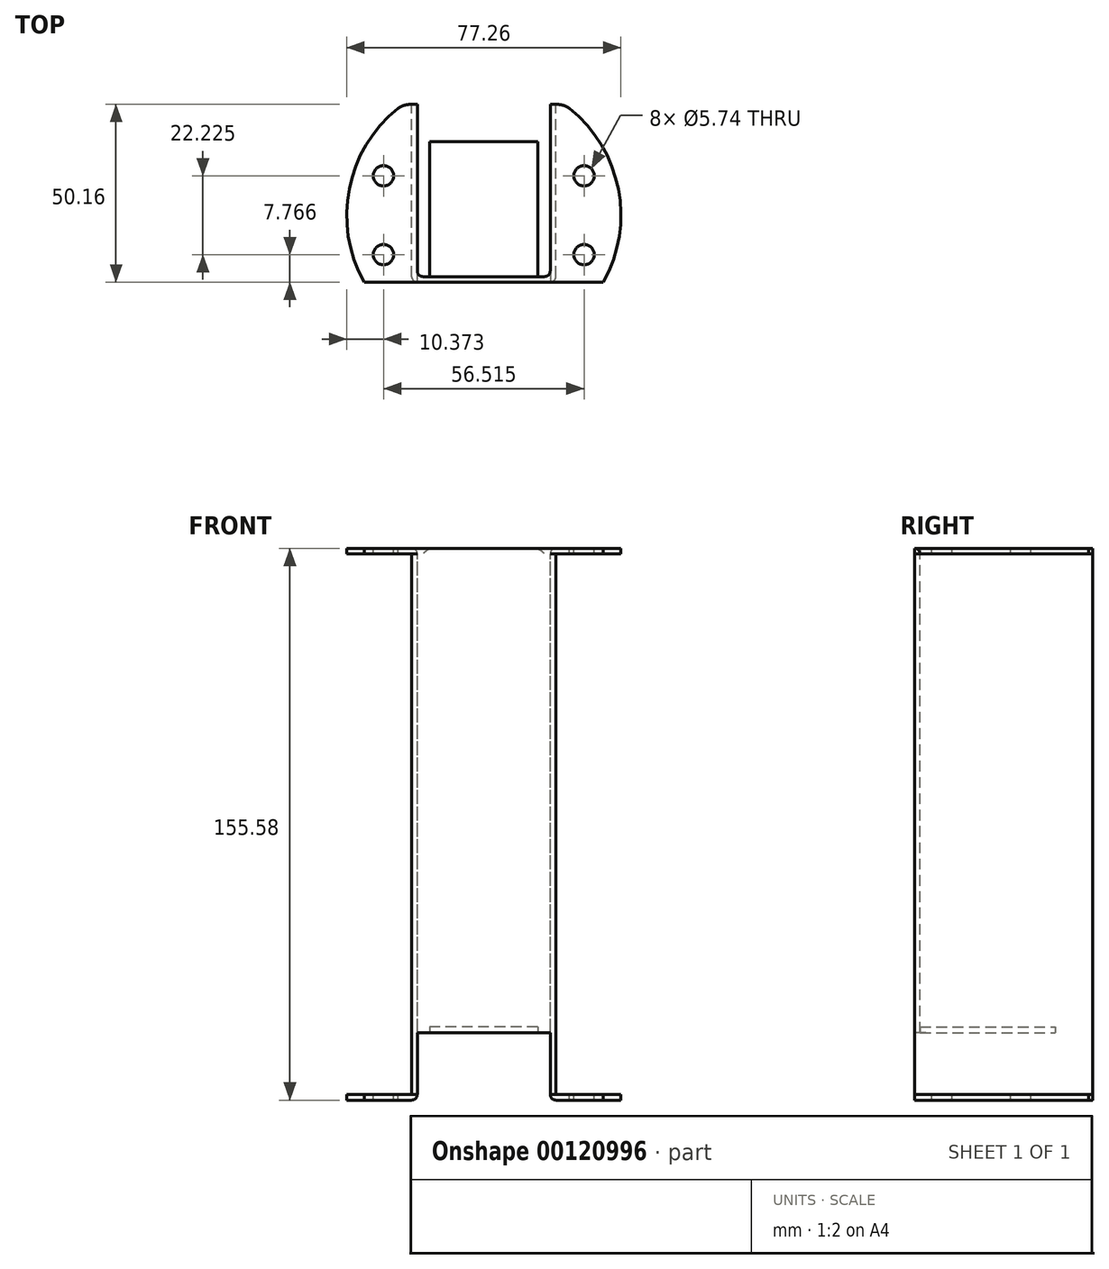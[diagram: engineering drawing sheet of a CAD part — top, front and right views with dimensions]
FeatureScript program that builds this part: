
annotation { "Feature Type Name" : "Feature", "Feature Type Description" : "" }
export const myFeature = defineFeature(function(context is Context, id is Id, definition is map)
    precondition{}
    {
        {
            var Q0;
            Q0=qCreatedBy(makeId("Top.planeOp"),FACE);
            var sketch = newSketch(context, id + "F0", { "sketchPlane" : qUnion([Q0])});
            skLineSegment(sketch, "E0", {"start": v(0, 0) * mm, "end": v(20.32, 0) * mm});
            skLineSegment(sketch, "E1", {"start": v(20.32, 0) * mm, "end": v(20.32, 50.17) * mm});
            skLineSegment(sketch, "E2", {"start": v(20.32, 50.17) * mm, "end": v(18.73, 50.17) * mm});
            skLineSegment(sketch, "E3", {"start": v(18.73, 50.17) * mm, "end": v(18.73, 1.59) * mm});
            skLineSegment(sketch, "E4", {"start": v(18.73, 1.59) * mm, "end": v(-18.73, 1.59) * mm});
            skLineSegment(sketch, "E5", {"start": v(-18.73, 1.59) * mm, "end": v(-18.73, 50.16) * mm});
            skLineSegment(sketch, "E6", {"start": v(-18.73, 50.16) * mm, "end": v(-20.32, 50.16) * mm});
            skLineSegment(sketch, "E7", {"start": v(-20.32, 50.17) * mm, "end": v(-20.32, 0) * mm});
            skLineSegment(sketch, "E8", {"start": v(-20.32, 0) * mm, "end": v(0, 0) * mm});
            skLineSegment(sketch, "E9", {"start": v(18.73, 1.59) * mm, "end": v(18.73, 0) * mm, "construction": true});
            skLineSegment(sketch, "E10", {"start": v(20.32, 0) * mm, "end": v(33.7, 0) * mm});
            skLineSegment(sketch, "E11", {"start": v(20.32, 49.04) * mm, "end": v(24.14, 49.04) * mm});
            skArc(sketch, "E12", {"start": v(33.7, 0) * mm, "mid": v(37.92, 26.27) * mm, "end": v(24.14, 49.04) * mm});
            skCircle(sketch, "E13", {"center": v(28.26, 30) * mm, "radius": 2.87 * mm});
            skCircle(sketch, "E14", {"center": v(28.26, 7.77) * mm, "radius": 2.87 * mm});
            skLineSegment(sketch, "E15", {"start": v(28.26, 30) * mm, "end": v(28.26, 7.77) * mm, "construction": true});
            skLineSegment(sketch, "E16", {"start": v(38.63, 18.88) * mm, "end": v(20.32, 18.88) * mm, "construction": true});
            skLineSegment(sketch, "E17", {"start": v(38.63, 18.88) * mm, "end": v(38.63, 5.02) * mm, "construction": true});
            skPoint(sketch, "E18", {"position": v(28.26, 18.88) * mm});
            skArc(sketch, "E19", {"start": v(24.14, 49.04) * mm, "mid": v(22.31, 49.88) * mm, "end": v(20.32, 50.17) * mm});
            skSolve(sketch);
        }
        {
            var Q0;
            {var subQ3=sQuery(id+"F0.wireOp",EDGE,"E0");Q0=makeQuery(id+"F0.imprint","IMPRINT",FACE,{"disambiguationData":[TD([[makeQuery(id+"F0.imprint","IMPRINT",EDGE,{"derivedFrom":subQ3}),1.0]])]});}
            extrude(context, id + "F1", {"entities" : qUnion([Q0]), "oppositeDirection" : true, "depth" : 136.53 * mm});
        }
        {
            var Q0;
            Q0=makeQuery(id+"F1.opExtrude","CAP_FACE",FACE,{"disambiguationData":[OSD([sQuery(id+"F0.wireOp",EDGE,"E0"),sQuery(id+"F0.wireOp",EDGE,"E1"),sQuery(id+"F0.wireOp",EDGE,"E2"),sQuery(id+"F0.wireOp",EDGE,"E3"),sQuery(id+"F0.wireOp",EDGE,"E4"),sQuery(id+"F0.wireOp",EDGE,"E5"),sQuery(id+"F0.wireOp",EDGE,"E6"),sQuery(id+"F0.wireOp",EDGE,"E7"),sQuery(id+"F0.wireOp",EDGE,"E8")])],"isStart":false});
            var sketch = newSketch(context, id + "F2", { "sketchPlane" : qUnion([Q0])});
            skLineSegment(sketch, "E20.0.0", {"start": v(20.32, 0) * mm, "end": v(-20.32, 0) * mm});
            skLineSegment(sketch, "E20.0.1", {"start": v(-20.32, 0) * mm, "end": v(-20.32, -50.17) * mm});
            skLineSegment(sketch, "E20.0.2", {"start": v(-20.32, -50.16) * mm, "end": v(-18.73, -50.16) * mm});
            skLineSegment(sketch, "E20.0.3", {"start": v(-18.73, -50.17) * mm, "end": v(-18.73, -1.59) * mm});
            skLineSegment(sketch, "E20.0.4", {"start": v(-18.73, -1.59) * mm, "end": v(18.73, -1.59) * mm});
            skLineSegment(sketch, "E20.0.5", {"start": v(18.73, -1.59) * mm, "end": v(18.73, -50.17) * mm});
            skLineSegment(sketch, "E20.0.6", {"start": v(18.73, -50.17) * mm, "end": v(20.32, -50.17) * mm});
            skLineSegment(sketch, "E20.0.7", {"start": v(20.32, -50.17) * mm, "end": v(20.32, 0) * mm});
            skLineSegment(sketch, "E21", {"start": v(-18.73, -1.59) * mm, "end": v(-18.73, 0) * mm});
            skLineSegment(sketch, "E22", {"start": v(18.73, -1.59) * mm, "end": v(18.73, 0) * mm});
            skSolve(sketch);
        }
        {
            var Q0;
            {var subQ1=sQuery(id+"F2.wireOp",EDGE,"E20.0.1");Q0=makeQuery(id+"F2.imprint","IMPRINT",FACE,{"disambiguationData":[TD([[makeQuery(id+"F2.imprint","IMPRINT",EDGE,{"derivedFrom":subQ1}),-1.0]])]});}
            var Q1;
            Q1=makeQuery(id+"F2.imprint","IMPRINT",FACE,{"disambiguationData":[TD([[makeQuery(id+"F2.imprint","IMPRINT",EDGE,{"derivedFrom":sQuery(id+"F2.wireOp",EDGE,"E20.0.5")}),-1.0]])]});
            extrude(context, id + "F3", {"entities" : qUnion([Q0, Q1]), "operationType" : NewBodyOperationType.ADD, "depth" : 19.05 * mm});
        }
        {
            var Q0;
            {var subQ0=sQuery(id+"F0.wireOp",EDGE,"E10");Q0=makeQuery(id+"F0.imprint","IMPRINT",FACE,{"disambiguationData":[TD([[makeQuery(id+"F0.imprint","IMPRINT",EDGE,{"derivedFrom":subQ0}),1.0]])]});}
            var Q1;
            {var subQ2=sQuery(id+"F0.wireOp",EDGE,"E11");Q1=makeQuery(id+"F0.imprint","IMPRINT",FACE,{"disambiguationData":[TD([[makeQuery(id+"F0.imprint","IMPRINT",EDGE,{"derivedFrom":subQ2}),1.0]])]});}
            extrude(context, id + "F4", {"entities" : qUnion([Q0, Q1]), "oppositeDirection" : true, "depth" : 1.59 * mm});
        }
        {
            var Q0;
            Q0=makeQuery(id+"F4.opExtrude","SWEPT_BODY",BODY,{"disambiguationData":[OSD([sQuery(id+"F0.wireOp",EDGE,"E1"),sQuery(id+"F0.wireOp",EDGE,"E10"),sQuery(id+"F0.wireOp",EDGE,"E12"),sQuery(id+"F0.wireOp",EDGE,"E13"),sQuery(id+"F0.wireOp",EDGE,"E14"),sQuery(id+"F0.wireOp",EDGE,"E19")])]});
            var Q1;
            Q1=qCreatedBy(makeId("Right.planeOp"),FACE);
            mirror(context, id + "F5", {"entities" : qUnion([Q0]), "mirrorPlane" : qUnion([Q1])});
        }
        {
            var Q0;
            Q0=makeQuery(id+"F5.opPattern","COPY",BODY,{"derivedFrom":makeQuery(id+"F4.opExtrude","SWEPT_BODY",BODY,{"disambiguationData":[OSD([sQuery(id+"F0.wireOp",EDGE,"E1"),sQuery(id+"F0.wireOp",EDGE,"E10"),sQuery(id+"F0.wireOp",EDGE,"E12"),sQuery(id+"F0.wireOp",EDGE,"E13"),sQuery(id+"F0.wireOp",EDGE,"E14"),sQuery(id+"F0.wireOp",EDGE,"E19")])]}),"instanceName":"1"});
            var Q1;
            Q1=makeQuery(id+"F4.opExtrude","SWEPT_BODY",BODY,{"disambiguationData":[OSD([sQuery(id+"F0.wireOp",EDGE,"E1"),sQuery(id+"F0.wireOp",EDGE,"E10"),sQuery(id+"F0.wireOp",EDGE,"E12"),sQuery(id+"F0.wireOp",EDGE,"E13"),sQuery(id+"F0.wireOp",EDGE,"E14"),sQuery(id+"F0.wireOp",EDGE,"E19")])]});
            var Q2;
            Q2=makeQuery(id+"F5.opPattern","COPY",VERTEX,{"derivedFrom":makeQuery(id+"F4.opExtrude","CAP_VERTEX",VERTEX,{"disambiguationData":[OSD([sQuery(id+"F0.wireOp",EDGE,"E0"),sQuery(id+"F0.wireOp",EDGE,"E1"),sQuery(id+"F0.wireOp",EDGE,"E10")])],"isStart":false}),"instanceName":"1"});
            var Q3;
            Q3=makeQuery(id+"F3.opExtrude","CAP_VERTEX",VERTEX,{"disambiguationData":[OSD([sQuery(id+"F2.wireOp",EDGE,"E20.0.0"),sQuery(id+"F2.wireOp",EDGE,"E20.0.1")])],"isStart":false});
            var Q4;
            Q4=makeQuery(id+"F5.opPattern","COPY",VERTEX,{"derivedFrom":makeQuery(id+"F4.opExtrude","CAP_VERTEX",VERTEX,{"disambiguationData":[OSD([sQuery(id+"F0.wireOp",EDGE,"E0"),sQuery(id+"F0.wireOp",EDGE,"E1"),sQuery(id+"F0.wireOp",EDGE,"E10")])],"isStart":false}),"instanceName":"1"});
            var Q5;
            Q5=makeQuery(id+"F3.opExtrude","CAP_VERTEX",VERTEX,{"disambiguationData":[OSD([sQuery(id+"F2.wireOp",EDGE,"E20.0.0"),sQuery(id+"F2.wireOp",EDGE,"E20.0.1")])],"isStart":false});
            transform(context, id + "F6", {"entities" : qUnion([Q0, Q1]), "transformType" : TransformType.TRANSLATION_ENTITY, "oppositeDirectionEntity" : false, "transformLine" : qUnion([Q2, Q3]), "makeCopy" : true});
        }
        {
            var Q0;
            Q0=makeQuery(id+"F1.opExtrude","SWEPT_BODY",BODY,{"disambiguationData":[OSD([sQuery(id+"F0.wireOp",EDGE,"E0"),sQuery(id+"F0.wireOp",EDGE,"E1"),sQuery(id+"F0.wireOp",EDGE,"E2"),sQuery(id+"F0.wireOp",EDGE,"E3"),sQuery(id+"F0.wireOp",EDGE,"E4"),sQuery(id+"F0.wireOp",EDGE,"E5"),sQuery(id+"F0.wireOp",EDGE,"E6"),sQuery(id+"F0.wireOp",EDGE,"E7"),sQuery(id+"F0.wireOp",EDGE,"E8")])]});
            var Q1;
            Q1=makeQuery(id+"F4.opExtrude","SWEPT_BODY",BODY,{"disambiguationData":[OSD([sQuery(id+"F0.wireOp",EDGE,"E1"),sQuery(id+"F0.wireOp",EDGE,"E10"),sQuery(id+"F0.wireOp",EDGE,"E12"),sQuery(id+"F0.wireOp",EDGE,"E13"),sQuery(id+"F0.wireOp",EDGE,"E14"),sQuery(id+"F0.wireOp",EDGE,"E19")])]});
            var Q2;
            Q2=makeQuery(id+"F5.opPattern","COPY",BODY,{"derivedFrom":makeQuery(id+"F4.opExtrude","SWEPT_BODY",BODY,{"disambiguationData":[OSD([sQuery(id+"F0.wireOp",EDGE,"E1"),sQuery(id+"F0.wireOp",EDGE,"E10"),sQuery(id+"F0.wireOp",EDGE,"E12"),sQuery(id+"F0.wireOp",EDGE,"E13"),sQuery(id+"F0.wireOp",EDGE,"E14"),sQuery(id+"F0.wireOp",EDGE,"E19")])]}),"instanceName":"1"});
            var Q3;
            Q3=makeQuery(id+"F6.opPattern","COPY",BODY,{"derivedFrom":makeQuery(id+"F4.opExtrude","SWEPT_BODY",BODY,{"disambiguationData":[OSD([sQuery(id+"F0.wireOp",EDGE,"E1"),sQuery(id+"F0.wireOp",EDGE,"E10"),sQuery(id+"F0.wireOp",EDGE,"E12"),sQuery(id+"F0.wireOp",EDGE,"E13"),sQuery(id+"F0.wireOp",EDGE,"E14"),sQuery(id+"F0.wireOp",EDGE,"E19")])]}),"instanceName":"1"});
            var Q4;
            Q4=makeQuery(id+"F6.opPattern","COPY",BODY,{"derivedFrom":makeQuery(id+"F5.opPattern","COPY",BODY,{"derivedFrom":makeQuery(id+"F4.opExtrude","SWEPT_BODY",BODY,{"disambiguationData":[OSD([sQuery(id+"F0.wireOp",EDGE,"E1"),sQuery(id+"F0.wireOp",EDGE,"E10"),sQuery(id+"F0.wireOp",EDGE,"E12"),sQuery(id+"F0.wireOp",EDGE,"E13"),sQuery(id+"F0.wireOp",EDGE,"E14"),sQuery(id+"F0.wireOp",EDGE,"E19")])]}),"instanceName":"1"}),"instanceName":"1"});
            booleanBodies(context, id + "F7", {"operationType" : BooleanOperationType.UNION, "tools" : qUnion([Q0, Q1, Q2, Q3, Q4])});
        }
        {
            var Q0;
            Q0=makeQuery(id+"F1.opExtrude","CAP_FACE",FACE,{"disambiguationData":[OSD([sQuery(id+"F0.wireOp",EDGE,"E0"),sQuery(id+"F0.wireOp",EDGE,"E1"),sQuery(id+"F0.wireOp",EDGE,"E2"),sQuery(id+"F0.wireOp",EDGE,"E3"),sQuery(id+"F0.wireOp",EDGE,"E4"),sQuery(id+"F0.wireOp",EDGE,"E5"),sQuery(id+"F0.wireOp",EDGE,"E6"),sQuery(id+"F0.wireOp",EDGE,"E7"),sQuery(id+"F0.wireOp",EDGE,"E8")])],"isStart":false});
            var sketch = newSketch(context, id + "F8", { "sketchPlane" : qUnion([Q0])});
            skLineSegment(sketch, "E23.bottom", {"start": v(-15.24, -1.59) * mm, "end": v(15.24, -1.59) * mm});
            skLineSegment(sketch, "E23.top", {"start": v(-15.24, -39.69) * mm, "end": v(15.24, -39.69) * mm});
            skLineSegment(sketch, "E23.left", {"start": v(-15.24, -1.59) * mm, "end": v(-15.24, -39.69) * mm});
            skLineSegment(sketch, "E23.right", {"start": v(15.24, -1.59) * mm, "end": v(15.24, -39.69) * mm});
            skPoint(sketch, "E24", {"position": v(0, -1.59) * mm});
            skSolve(sketch);
        }
        {
            var Q0;
            Q0=makeQuery(id+"F8.imprint","IMPRINT",FACE,{"disambiguationData":[TD([[makeQuery(id+"F8.imprint","IMPRINT",EDGE,{"derivedFrom":sQuery(id+"F8.wireOp",EDGE,"E23.bottom")}),1.0]])]});
            extrude(context, id + "F9", {"entities" : qUnion([Q0]), "operationType" : NewBodyOperationType.ADD, "oppositeDirection" : true, "depth" : 1.59 * mm});
        }
        {
            var Q0;
            Q0=makeQuery(id+"F5.opPattern","COPY",EDGE,{"derivedFrom":makeQuery(id+"F4.opExtrude","CAP_EDGE",EDGE,{"disambiguationData":[OSD([sQuery(id+"F0.wireOp",EDGE,"E1")])],"isStart":false}),"instanceName":"1"});
            var Q1;
            Q1=makeQuery(id+"F1.opExtrude","CAP_EDGE",EDGE,{"disambiguationData":[OSD([sQuery(id+"F0.wireOp",EDGE,"E5")])],"isStart":true});
            var Q2;
            Q2=makeQuery(id+"F3.boolean.opBoolean","MERGE",EDGE,{"derivedFrom":[makeQuery(id+"F1.opExtrude","SWEPT_EDGE",EDGE,{"disambiguationData":[OSD([sQuery(id+"F0.wireOp",EDGE,"E7"),sQuery(id+"F0.wireOp",EDGE,"E8")])]}),makeQuery(id+"F3.opExtrude","SWEPT_EDGE",EDGE,{"disambiguationData":[OSD([sQuery(id+"F2.wireOp",EDGE,"E20.0.0"),sQuery(id+"F2.wireOp",EDGE,"E20.0.1")])]})]});
            var Q3;
            Q3=makeQuery(id+"F1.opExtrude","SWEPT_EDGE",EDGE,{"disambiguationData":[OSD([sQuery(id+"F0.wireOp",EDGE,"E4"),sQuery(id+"F0.wireOp",EDGE,"E5")])]});
            var Q4;
            Q4=makeQuery(id+"F1.opExtrude","CAP_EDGE",EDGE,{"disambiguationData":[OSD([sQuery(id+"F0.wireOp",EDGE,"E3")])],"isStart":true});
            var Q5;
            Q5=makeQuery(id+"F4.opExtrude","CAP_EDGE",EDGE,{"disambiguationData":[OSD([sQuery(id+"F0.wireOp",EDGE,"E1")])],"isStart":false});
            var Q6;
            Q6=makeQuery(id+"F3.boolean.opBoolean","MERGE",EDGE,{"derivedFrom":[makeQuery(id+"F1.opExtrude","SWEPT_EDGE",EDGE,{"disambiguationData":[OSD([sQuery(id+"F0.wireOp",EDGE,"E0"),sQuery(id+"F0.wireOp",EDGE,"E1"),sQuery(id+"F0.wireOp",EDGE,"E10")])]}),makeQuery(id+"F3.opExtrude","SWEPT_EDGE",EDGE,{"disambiguationData":[OSD([sQuery(id+"F2.wireOp",EDGE,"E20.0.0"),sQuery(id+"F2.wireOp",EDGE,"E20.0.7")])]})]});
            var Q7;
            Q7=makeQuery(id+"F1.opExtrude","SWEPT_EDGE",EDGE,{"disambiguationData":[OSD([sQuery(id+"F0.wireOp",EDGE,"E3"),sQuery(id+"F0.wireOp",EDGE,"E4")])]});
            var Q8;
            Q8=makeQuery(id+"F6.opPattern","COPY",EDGE,{"derivedFrom":makeQuery(id+"F4.opExtrude","CAP_EDGE",EDGE,{"disambiguationData":[OSD([sQuery(id+"F0.wireOp",EDGE,"E1")])],"isStart":true}),"instanceName":"1"});
            var Q9;
            Q9=makeQuery(id+"F3.opExtrude","CAP_EDGE",EDGE,{"disambiguationData":[OSD([sQuery(id+"F2.wireOp",EDGE,"E20.0.5"),sQuery(id+"F2.wireOp",EDGE,"E22")])],"isStart":false});
            var Q10;
            Q10=makeQuery(id+"F3.opExtrude","CAP_EDGE",EDGE,{"disambiguationData":[OSD([sQuery(id+"F2.wireOp",EDGE,"E20.0.3"),sQuery(id+"F2.wireOp",EDGE,"E21")])],"isStart":false});
            var Q11;
            Q11=makeQuery(id+"F6.opPattern","COPY",EDGE,{"derivedFrom":makeQuery(id+"F5.opPattern","COPY",EDGE,{"derivedFrom":makeQuery(id+"F4.opExtrude","CAP_EDGE",EDGE,{"disambiguationData":[OSD([sQuery(id+"F0.wireOp",EDGE,"E1")])],"isStart":true}),"instanceName":"1"}),"instanceName":"1"});
            var Q12;
            Q12=makeQuery(id+"F9.opExtrude","CAP_EDGE",EDGE,{"disambiguationData":[OSD([sQuery(id+"F8.wireOp",EDGE,"E23.bottom")])],"isStart":false});
            fillet(context, id + "F10", {"entities" : qUnion([Q0, Q1, Q2, Q3, Q4, Q5, Q6, Q7, Q8, Q9, Q10, Q11, Q12]), "radius" : 1.59 * mm, "allowEdgeOverflow" : false});
        }
    });
